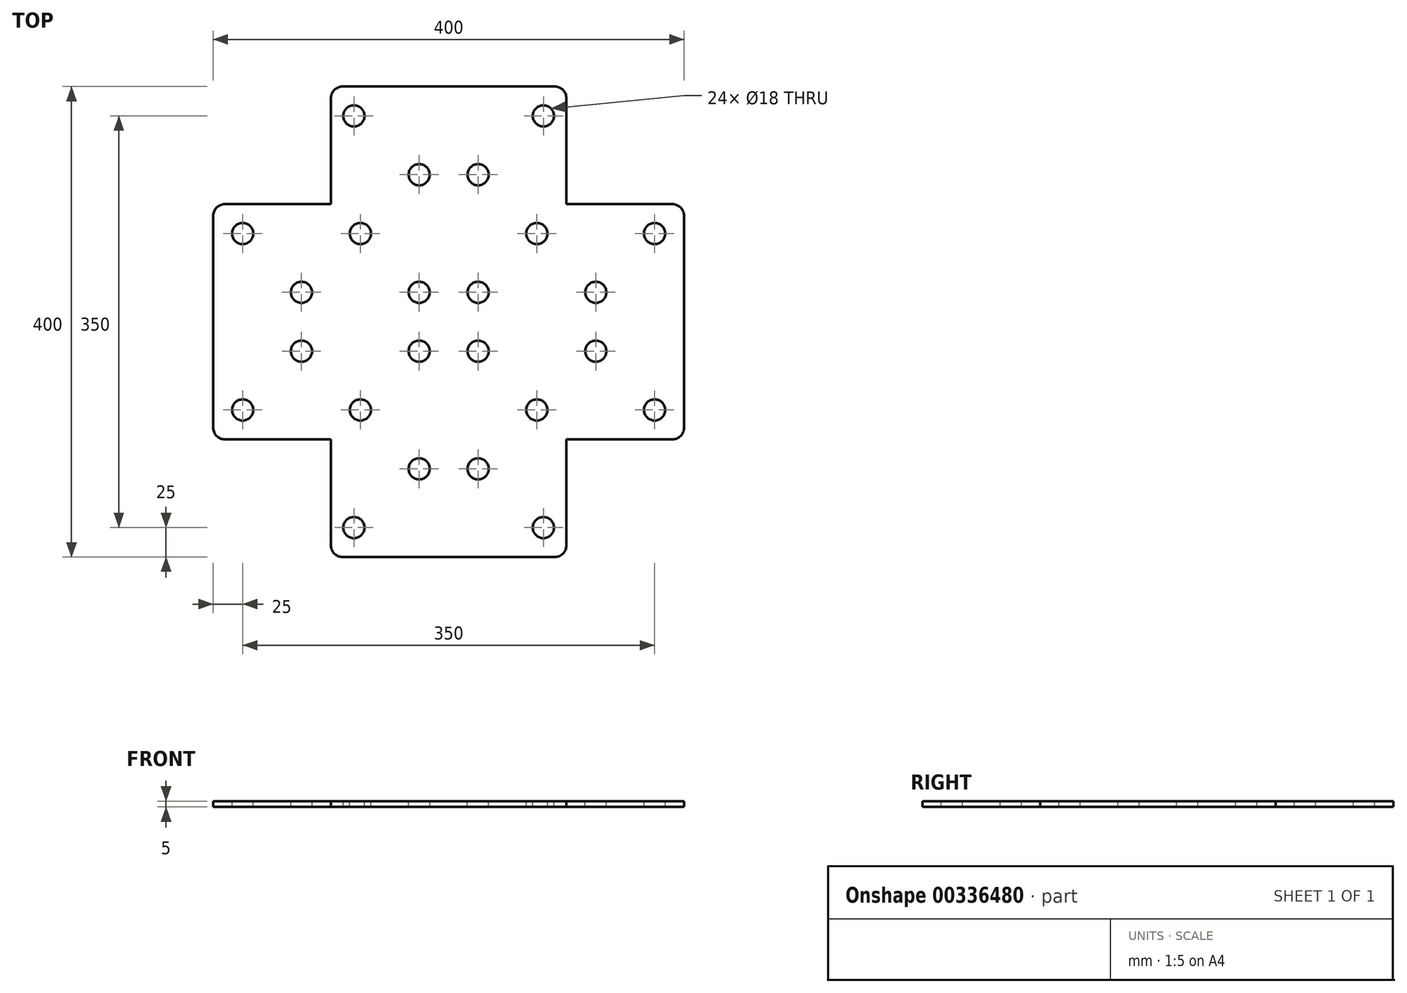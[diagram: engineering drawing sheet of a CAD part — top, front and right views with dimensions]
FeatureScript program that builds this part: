
annotation { "Feature Type Name" : "Feature", "Feature Type Description" : "" }
export const myFeature = defineFeature(function(context is Context, id is Id, definition is map)
    precondition{}
    {
        {
            var Q0;
            Q0=qCreatedBy(makeId("Top.planeOp"),FACE);
            var sketch = newSketch(context, id + "F0", { "sketchPlane" : qUnion([Q0])});
            skLineSegment(sketch, "E0", {"start": v(0, -200) * mm, "end": v(100, -200) * mm});
            skLineSegment(sketch, "E1", {"start": v(100, -200) * mm, "end": v(100, -100) * mm});
            skLineSegment(sketch, "E2", {"start": v(100, -100) * mm, "end": v(200, -100) * mm});
            skLineSegment(sketch, "E3", {"start": v(200, -100) * mm, "end": v(200, 0) * mm});
            skLineSegment(sketch, "E4.MirrorCS", {"start": v(100, 200) * mm, "end": v(100, 100) * mm});
            skLineSegment(sketch, "E5.MirrorCS", {"start": v(0, 200) * mm, "end": v(100, 200) * mm});
            skLineSegment(sketch, "E6.MirrorCS", {"start": v(100, 100) * mm, "end": v(200, 100) * mm});
            skLineSegment(sketch, "E7.MirrorCS", {"start": v(200, 100) * mm, "end": v(200, 0) * mm});
            skLineSegment(sketch, "E8.MirrorCS", {"start": v(0, -200) * mm, "end": v(-100, -200) * mm});
            skLineSegment(sketch, "E9.MirrorCS", {"start": v(-100, -200) * mm, "end": v(-100, -100) * mm});
            skLineSegment(sketch, "E10.MirrorCS", {"start": v(-100, -100) * mm, "end": v(-200, -100) * mm});
            skLineSegment(sketch, "E11.MirrorCS", {"start": v(-100, 100) * mm, "end": v(-200, 100) * mm});
            skLineSegment(sketch, "E12.MirrorCS", {"start": v(-200, 100) * mm, "end": v(-200, 0) * mm});
            skLineSegment(sketch, "E13.MirrorCS", {"start": v(-200, -100) * mm, "end": v(-200, 0) * mm});
            skLineSegment(sketch, "E14.MirrorCS", {"start": v(-100, 200) * mm, "end": v(-100, 100) * mm});
            skLineSegment(sketch, "E15.MirrorCS", {"start": v(0, 200) * mm, "end": v(-100, 200) * mm});
            skSolve(sketch);
        }
        {
            var Q0;
            Q0=makeQuery(id+"F0.imprint","IMPRINT",FACE,{"disambiguationData":[TD([[makeQuery(id+"F0.imprint","IMPRINT",EDGE,{"derivedFrom":sQuery(id+"F0.wireOp",EDGE,"E0")}),1.0]])]});
            extrude(context, id + "F1", {"entities" : qUnion([Q0]), "depth" : 5 * mm});
        }
        {
            var Q0;
            Q0=makeQuery(id+"F1.opExtrude","CAP_FACE",FACE,{"disambiguationData":[OSD([sQuery(id+"F0.wireOp",EDGE,"E0"),sQuery(id+"F0.wireOp",EDGE,"E1"),sQuery(id+"F0.wireOp",EDGE,"E2"),sQuery(id+"F0.wireOp",EDGE,"E3"),sQuery(id+"F0.wireOp",EDGE,"E4.MirrorCS"),sQuery(id+"F0.wireOp",EDGE,"E5.MirrorCS"),sQuery(id+"F0.wireOp",EDGE,"E6.MirrorCS"),sQuery(id+"F0.wireOp",EDGE,"E7.MirrorCS"),sQuery(id+"F0.wireOp",EDGE,"E8.MirrorCS"),sQuery(id+"F0.wireOp",EDGE,"E9.MirrorCS"),sQuery(id+"F0.wireOp",EDGE,"E10.MirrorCS"),sQuery(id+"F0.wireOp",EDGE,"E11.MirrorCS"),sQuery(id+"F0.wireOp",EDGE,"E12.MirrorCS"),sQuery(id+"F0.wireOp",EDGE,"E13.MirrorCS"),sQuery(id+"F0.wireOp",EDGE,"E14.MirrorCS"),sQuery(id+"F0.wireOp",EDGE,"E15.MirrorCS")])],"isStart":false});
            var sketch = newSketch(context, id + "F2", { "sketchPlane" : qUnion([Q0])});
            skCircle(sketch, "E16", {"center": v(25, 25) * mm, "radius": 9 * mm});
            skCircle(sketch, "E17.1.1.0", {"center": v(75, 75) * mm, "radius": 9 * mm});
            skCircle(sketch, "E17.2.0.0", {"center": v(125, 25) * mm, "radius": 9 * mm});
            skCircle(sketch, "E17.3.1.0", {"center": v(175, 75) * mm, "radius": 9 * mm});
            skCircle(sketch, "E18.0.1.1", {"center": v(25, 125) * mm, "radius": 9 * mm});
            skCircle(sketch, "E18.0.1.4", {"center": v(80.5, 175) * mm, "radius": 9 * mm});
            skCircle(sketch, "E19.MirrorC", {"center": v(80.5, -175) * mm, "radius": 9 * mm});
            skCircle(sketch, "E20.MirrorC", {"center": v(25, -125) * mm, "radius": 9 * mm});
            skCircle(sketch, "E21.MirrorC", {"center": v(175, -75) * mm, "radius": 9 * mm});
            skCircle(sketch, "E22.MirrorC", {"center": v(75, -75) * mm, "radius": 9 * mm});
            skCircle(sketch, "E23.MirrorC", {"center": v(125, -25) * mm, "radius": 9 * mm});
            skCircle(sketch, "E24.MirrorC", {"center": v(25, -25) * mm, "radius": 9 * mm});
            skCircle(sketch, "E25.MirrorC", {"center": v(-25, -125) * mm, "radius": 9 * mm});
            skCircle(sketch, "E26.MirrorC", {"center": v(-175, 75) * mm, "radius": 9 * mm});
            skCircle(sketch, "E27.MirrorC", {"center": v(-175, -75) * mm, "radius": 9 * mm});
            skCircle(sketch, "E28.MirrorC", {"center": v(-80.5, 175) * mm, "radius": 9 * mm});
            skCircle(sketch, "E29.MirrorC", {"center": v(-25, 25) * mm, "radius": 9 * mm});
            skCircle(sketch, "E30.MirrorC", {"center": v(-125, 25) * mm, "radius": 9 * mm});
            skCircle(sketch, "E31.MirrorC", {"center": v(-125, -25) * mm, "radius": 9 * mm});
            skCircle(sketch, "E32.MirrorC", {"center": v(-80.5, -175) * mm, "radius": 9 * mm});
            skCircle(sketch, "E33.MirrorC", {"center": v(-25, -25) * mm, "radius": 9 * mm});
            skCircle(sketch, "E34.MirrorC", {"center": v(-25, 125) * mm, "radius": 9 * mm});
            skCircle(sketch, "E35.MirrorC", {"center": v(-75, 75) * mm, "radius": 9 * mm});
            skCircle(sketch, "E36.MirrorC", {"center": v(-75, -75) * mm, "radius": 9 * mm});
            skSolve(sketch);
        }
        {
            var Q0;
            Q0 = qSketchRegion(id + "F2", true);
            extrude(context, id + "F3", {"entities" : qUnion([Q0]), "operationType" : NewBodyOperationType.REMOVE, "oppositeDirection" : true, "depth" : 25 * mm});
        }
        {
            var Q0;
            Q0=makeQuery(id+"F1.opExtrude","SWEPT_EDGE",EDGE,{"disambiguationData":[OSD([sQuery(id+"F0.wireOp",EDGE,"E0"),sQuery(id+"F0.wireOp",EDGE,"E1")])]});
            var Q1;
            Q1=makeQuery(id+"F1.opExtrude","SWEPT_EDGE",EDGE,{"disambiguationData":[OSD([sQuery(id+"F0.wireOp",EDGE,"E8.MirrorCS"),sQuery(id+"F0.wireOp",EDGE,"E9.MirrorCS")])]});
            var Q2;
            Q2=makeQuery(id+"F1.opExtrude","SWEPT_EDGE",EDGE,{"disambiguationData":[OSD([sQuery(id+"F0.wireOp",EDGE,"E10.MirrorCS"),sQuery(id+"F0.wireOp",EDGE,"E13.MirrorCS")])]});
            var Q3;
            Q3=makeQuery(id+"F1.opExtrude","SWEPT_EDGE",EDGE,{"disambiguationData":[OSD([sQuery(id+"F0.wireOp",EDGE,"E11.MirrorCS"),sQuery(id+"F0.wireOp",EDGE,"E12.MirrorCS")])]});
            var Q4;
            Q4=makeQuery(id+"F1.opExtrude","SWEPT_EDGE",EDGE,{"disambiguationData":[OSD([sQuery(id+"F0.wireOp",EDGE,"E14.MirrorCS"),sQuery(id+"F0.wireOp",EDGE,"E15.MirrorCS")])]});
            var Q5;
            Q5=makeQuery(id+"F1.opExtrude","SWEPT_EDGE",EDGE,{"disambiguationData":[OSD([sQuery(id+"F0.wireOp",EDGE,"E4.MirrorCS"),sQuery(id+"F0.wireOp",EDGE,"E5.MirrorCS")])]});
            var Q6;
            Q6=makeQuery(id+"F1.opExtrude","SWEPT_EDGE",EDGE,{"disambiguationData":[OSD([sQuery(id+"F0.wireOp",EDGE,"E6.MirrorCS"),sQuery(id+"F0.wireOp",EDGE,"E7.MirrorCS")])]});
            var Q7;
            Q7=makeQuery(id+"F1.opExtrude","SWEPT_EDGE",EDGE,{"disambiguationData":[OSD([sQuery(id+"F0.wireOp",EDGE,"E2"),sQuery(id+"F0.wireOp",EDGE,"E3")])]});
            fillet(context, id + "F4", {"entities" : qUnion([Q0, Q1, Q2, Q3, Q4, Q5, Q6, Q7]), "radius" : 10 * mm, "tangentPropagation" : true, "allowEdgeOverflow" : false});
        }
    });
